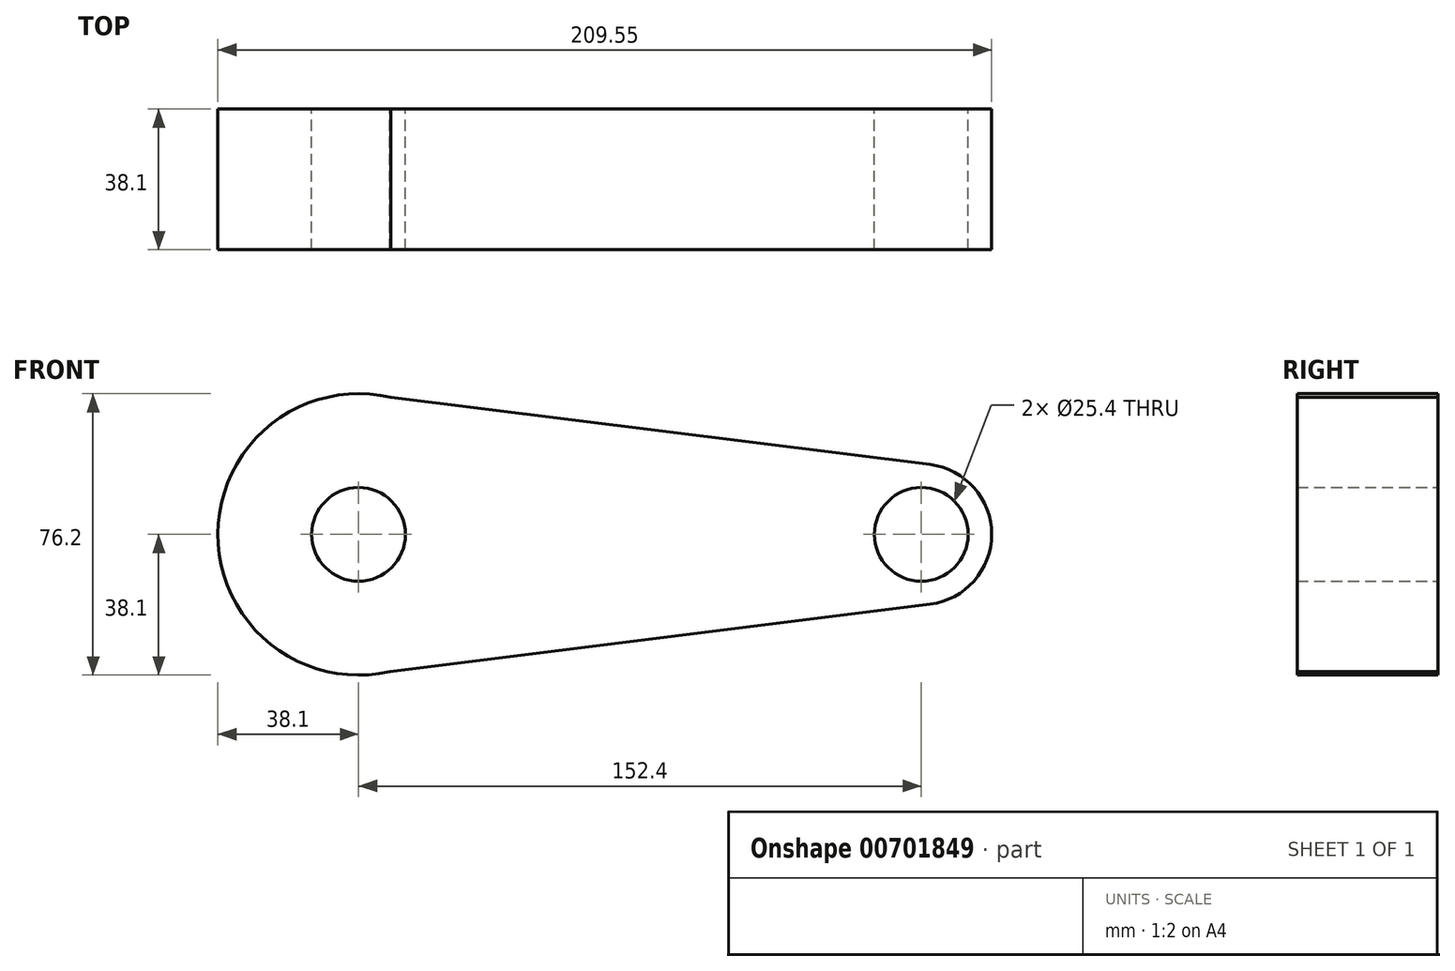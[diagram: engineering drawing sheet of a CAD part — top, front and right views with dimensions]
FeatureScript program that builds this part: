
annotation { "Feature Type Name" : "Feature", "Feature Type Description" : "" }
export const myFeature = defineFeature(function(context is Context, id is Id, definition is map)
    precondition{}
    {
        {
            var Q0;
            Q0=qCreatedBy(makeId("Front.planeOp"),FACE);
            var sketch = newSketch(context, id + "F0", { "sketchPlane" : qUnion([Q0])});
            skCircle(sketch, "E0", {"center": v(-85.3, 0) * mm, "radius": 38.1 * mm});
            skCircle(sketch, "E1", {"center": v(67.1, 0) * mm, "radius": 19.05 * mm});
            skLineSegment(sketch, "E2", {"start": v(-84.7, 38.1) * mm, "end": v(69.45, 18.9) * mm});
            skLineSegment(sketch, "E3", {"start": v(-84.4, -38.09) * mm, "end": v(69.46, -18.9) * mm});
            skCircle(sketch, "E4", {"center": v(-85.3, 0) * mm, "radius": 12.7 * mm});
            skCircle(sketch, "E5", {"center": v(67.1, 0) * mm, "radius": 12.7 * mm});
            skSolve(sketch);
        }
        {
            var Q0;
            Q0 = qSketchRegion(id + "F0", true);
            extrude(context, id + "F1", {"entities" : qUnion([Q0]), "depth" : 38.1 * mm, "offsetDistance" : 25.4 * mm});
        }
    });
